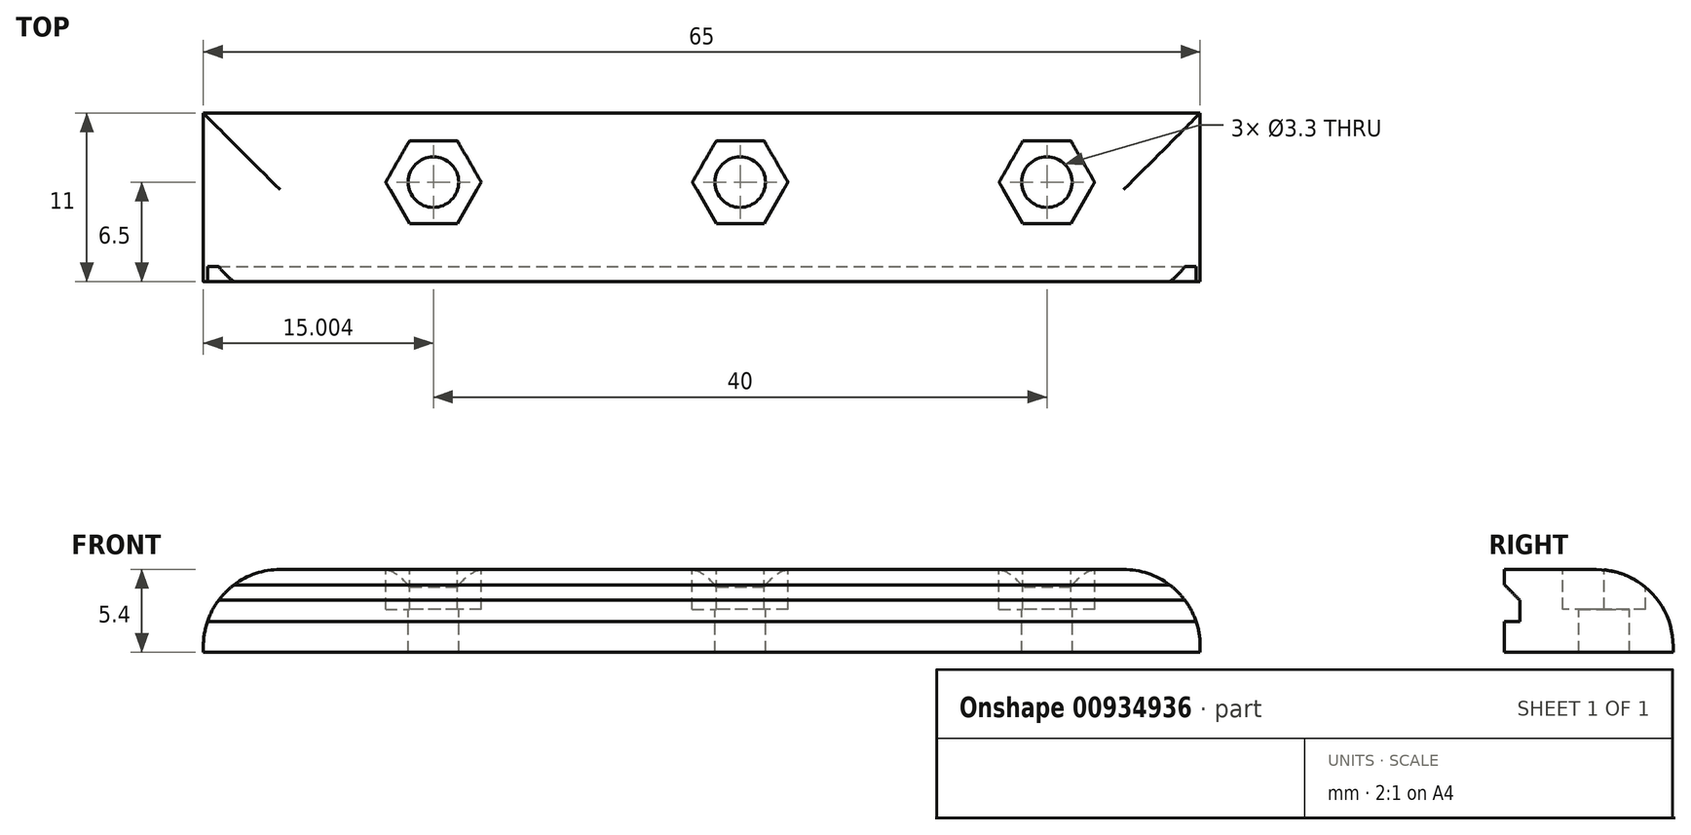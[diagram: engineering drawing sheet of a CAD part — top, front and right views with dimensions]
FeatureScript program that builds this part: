
annotation { "Feature Type Name" : "Feature", "Feature Type Description" : "" }
export const myFeature = defineFeature(function(context is Context, id is Id, definition is map)
    precondition{}
    {
        {
            var Q0;
            Q0=qCreatedBy(makeId("Front.planeOp"),FACE);
            var sketch = newSketch(context, id + "F0", { "sketchPlane" : qUnion([Q0])});
            skLineSegment(sketch, "E0.bottom", {"start": v(-0.35, 19.23) * mm, "end": v(64.65, 19.23) * mm});
            skLineSegment(sketch, "E0.top", {"start": v(-0.35, 13.83) * mm, "end": v(64.65, 13.83) * mm});
            skLineSegment(sketch, "E0.left", {"start": v(-0.35, 19.23) * mm, "end": v(-0.35, 13.83) * mm});
            skLineSegment(sketch, "E0.right", {"start": v(64.65, 19.23) * mm, "end": v(64.65, 13.83) * mm});
            skSolve(sketch);
        }
        {
            var Q0;
            Q0 = qSketchRegion(id + "F0", true);
            extrude(context, id + "F1", {"entities" : qUnion([Q0]), "depth" : 11 * mm, "offsetDistance" : 25 * mm});
        }
        {
            var Q0;
            Q0=makeQuery(id+"F1.opExtrude","CAP_FACE",FACE,{"disambiguationData":[OSD([sQuery(id+"F0.wireOp",EDGE,"E0.bottom"),sQuery(id+"F0.wireOp",EDGE,"E0.top"),sQuery(id+"F0.wireOp",EDGE,"E0.left"),sQuery(id+"F0.wireOp",EDGE,"E0.right")])],"isStart":false});
            var sketch = newSketch(context, id + "F2", { "sketchPlane" : qUnion([Q0])});
            skLineSegment(sketch, "E1.bottom", {"start": v(-0.35, 15.83) * mm, "end": v(64.65, 15.83) * mm});
            skLineSegment(sketch, "E1.top", {"start": v(-0.35, 17.23) * mm, "end": v(64.65, 17.23) * mm});
            skLineSegment(sketch, "E1.left", {"start": v(-0.35, 15.83) * mm, "end": v(-0.35, 17.23) * mm});
            skLineSegment(sketch, "E1.right", {"start": v(64.65, 15.83) * mm, "end": v(64.65, 17.23) * mm});
            skSolve(sketch);
        }
        {
            var Q0;
            Q0=makeQuery(id+"F2.imprint","IMPRINT",FACE,{"disambiguationData":[TD([[makeQuery(id+"F2.imprint","IMPRINT",EDGE,{"derivedFrom":sQuery(id+"F2.wireOp",EDGE,"E1.bottom")}),1.0]])]});
            extrude(context, id + "F3", {"entities" : qUnion([Q0]), "operationType" : NewBodyOperationType.REMOVE, "oppositeDirection" : true, "depth" : 1 * mm, "offsetDistance" : 25 * mm});
        }
        {
            var Q0;
            Q0=makeQuery(id+"F1.opExtrude","SWEPT_FACE",FACE,{"disambiguationData":[OSD([sQuery(id+"F0.wireOp",EDGE,"E0.bottom")])]});
            var sketch = newSketch(context, id + "F4", { "sketchPlane" : qUnion([Q0])});
            skCircle(sketch, "E2", {"center": v(14.65, -4.5) * mm, "radius": 1.65 * mm});
            skCircle(sketch, "E3.1.0.0", {"center": v(34.65, -4.5) * mm, "radius": 1.65 * mm});
            skCircle(sketch, "E3.2.0.0", {"center": v(54.65, -4.5) * mm, "radius": 1.65 * mm});
            skLineSegment(sketch, "E3.direction1", {"start": v(14.65, -4.5) * mm, "end": v(34.65, -4.5) * mm, "construction": true});
            skSolve(sketch);
        }
        {
            var Q0;
            Q0 = qSketchRegion(id + "F4", true);
            extrude(context, id + "F5", {"entities" : qUnion([Q0]), "operationType" : NewBodyOperationType.REMOVE, "oppositeDirection" : true, "depth" : 25 * mm, "offsetDistance" : 25 * mm});
        }
        {
            var Q0;
            Q0=makeQuery(id+"F1.opExtrude","SWEPT_FACE",FACE,{"disambiguationData":[OSD([sQuery(id+"F0.wireOp",EDGE,"E0.bottom")])]});
            var sketch = newSketch(context, id + "F6", { "sketchPlane" : qUnion([Q0])});
            skCircle(sketch, "E4.cCircle", {"center": v(14.65, -4.5) * mm, "radius": 2.7 * mm, "construction": true});
            skLineSegment(sketch, "E4.0", {"start": v(16.21, -7.2) * mm, "end": v(13.1, -7.2) * mm});
            skLineSegment(sketch, "E4.1", {"start": v(13.1, -7.2) * mm, "end": v(11.54, -4.5) * mm});
            skLineSegment(sketch, "E4.2", {"start": v(11.54, -4.5) * mm, "end": v(13.1, -1.8) * mm});
            skLineSegment(sketch, "E4.3", {"start": v(13.1, -1.8) * mm, "end": v(16.21, -1.8) * mm});
            skLineSegment(sketch, "E4.4", {"start": v(16.21, -1.8) * mm, "end": v(17.77, -4.5) * mm});
            skLineSegment(sketch, "E4.5", {"start": v(17.77, -4.5) * mm, "end": v(16.21, -7.2) * mm});
            skPoint(sketch, "E4.0.midPoint", {"position": v(14.65, -7.2) * mm});
            skCircle(sketch, "E5.cCircle", {"center": v(34.65, -4.5) * mm, "radius": 2.7 * mm, "construction": true});
            skLineSegment(sketch, "E5.0", {"start": v(36.21, -7.2) * mm, "end": v(33.1, -7.2) * mm});
            skLineSegment(sketch, "E5.1", {"start": v(33.1, -7.2) * mm, "end": v(31.54, -4.5) * mm});
            skLineSegment(sketch, "E5.2", {"start": v(31.54, -4.5) * mm, "end": v(33.1, -1.8) * mm});
            skLineSegment(sketch, "E5.3", {"start": v(33.1, -1.8) * mm, "end": v(36.21, -1.8) * mm});
            skLineSegment(sketch, "E5.4", {"start": v(36.21, -1.8) * mm, "end": v(37.77, -4.5) * mm});
            skLineSegment(sketch, "E5.5", {"start": v(37.77, -4.5) * mm, "end": v(36.21, -7.2) * mm});
            skPoint(sketch, "E5.0.midPoint", {"position": v(34.65, -7.2) * mm});
            skCircle(sketch, "E6.cCircle", {"center": v(54.65, -4.5) * mm, "radius": 2.7 * mm, "construction": true});
            skLineSegment(sketch, "E6.0", {"start": v(56.21, -7.2) * mm, "end": v(53.1, -7.2) * mm});
            skLineSegment(sketch, "E6.1", {"start": v(53.1, -7.2) * mm, "end": v(51.54, -4.5) * mm});
            skLineSegment(sketch, "E6.2", {"start": v(51.54, -4.5) * mm, "end": v(53.1, -1.8) * mm});
            skLineSegment(sketch, "E6.3", {"start": v(53.1, -1.8) * mm, "end": v(56.21, -1.8) * mm});
            skLineSegment(sketch, "E6.4", {"start": v(56.21, -1.8) * mm, "end": v(57.77, -4.5) * mm});
            skLineSegment(sketch, "E6.5", {"start": v(57.77, -4.5) * mm, "end": v(56.21, -7.2) * mm});
            skPoint(sketch, "E6.0.midPoint", {"position": v(54.65, -7.2) * mm});
            skSolve(sketch);
        }
        {
            var Q0;
            Q0 = qSketchRegion(id + "F6", true);
            extrude(context, id + "F7", {"entities" : qUnion([Q0]), "operationType" : NewBodyOperationType.REMOVE, "oppositeDirection" : true, "depth" : 2.6 * mm, "offsetDistance" : 25 * mm});
        }
        {
            var Q0;
            Q0=makeQuery(id+"F1.opExtrude","SWEPT_EDGE",EDGE,{"disambiguationData":[OSD([sQuery(id+"F0.wireOp",EDGE,"E0.bottom"),sQuery(id+"F0.wireOp",EDGE,"E0.right")])]});
            var Q1;
            Q1=makeQuery(id+"F1.opExtrude","CAP_EDGE",EDGE,{"disambiguationData":[OSD([sQuery(id+"F0.wireOp",EDGE,"E0.bottom")])],"isStart":true});
            var Q2;
            Q2=makeQuery(id+"F1.opExtrude","SWEPT_EDGE",EDGE,{"disambiguationData":[OSD([sQuery(id+"F0.wireOp",EDGE,"E0.bottom"),sQuery(id+"F0.wireOp",EDGE,"E0.left")])]});
            fillet(context, id + "F8", {"entities" : qUnion([Q0, Q1, Q2]), "radius" : 5 * mm, "tangentPropagation" : true, "allowEdgeOverflow" : false});
        }
        {
            var Q0;
            Q0=makeQuery(id+"F3.boolean.opBoolean","COPY",EDGE,{"derivedFrom":makeQuery(id+"F3.opExtrude","CAP_EDGE",EDGE,{"disambiguationData":[OSD([sQuery(id+"F2.wireOp",EDGE,"E1.top")])],"isStart":true})});
            chamfer(context, id + "F9", {"entities" : qUnion([Q0]), "width" : 1 * mm, "tangentPropagation" : true});
        }
    });
